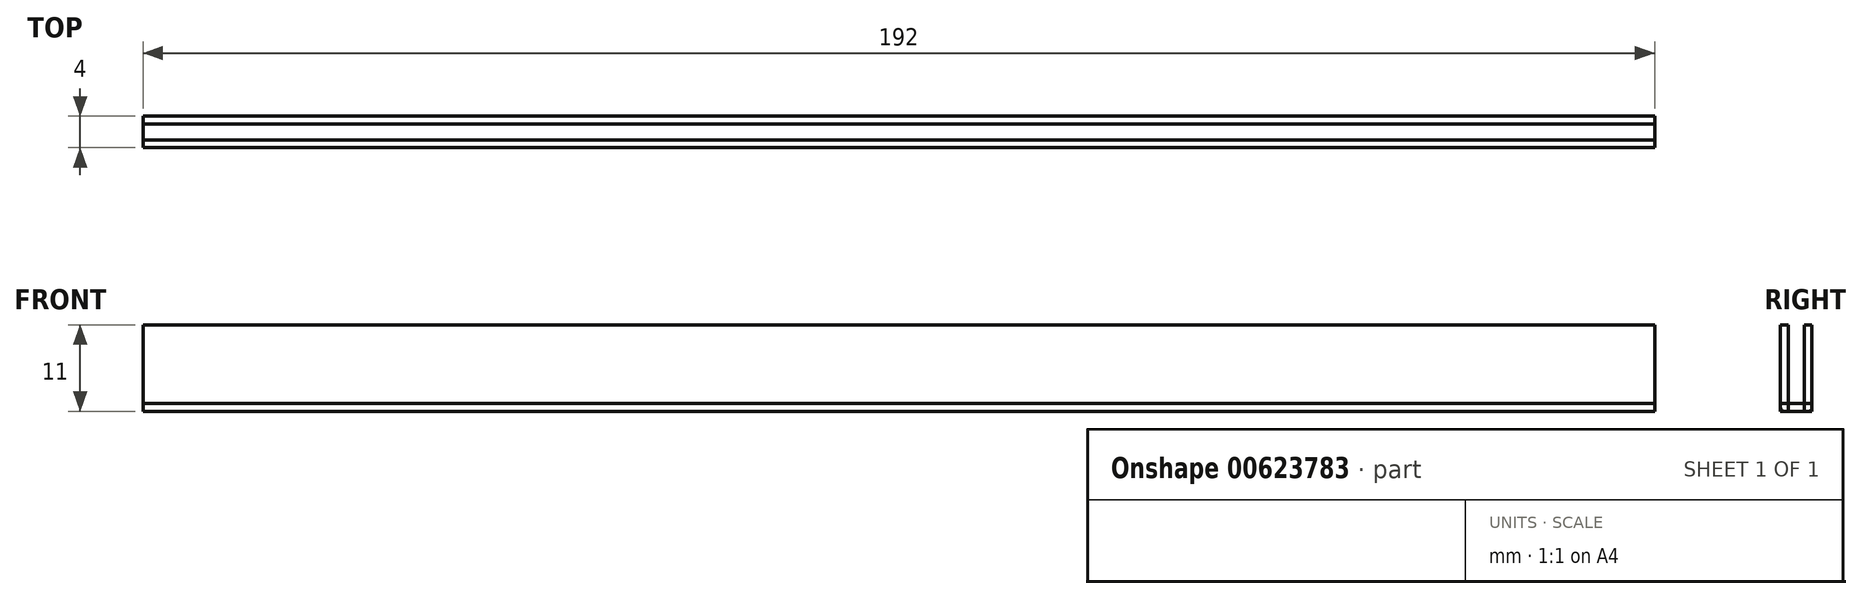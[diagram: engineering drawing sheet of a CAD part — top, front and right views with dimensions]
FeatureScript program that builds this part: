
annotation { "Feature Type Name" : "Feature", "Feature Type Description" : "" }
export const myFeature = defineFeature(function(context is Context, id is Id, definition is map)
    precondition{}
    {
        {
            var Q0;
            Q0=qCreatedBy(makeId("Top.planeOp"),FACE);
            var sketch = newSketch(context, id + "F0", { "sketchPlane" : qUnion([Q0])});
            skLineSegment(sketch, "E0.bottom", {"start": v(-97, -10) * mm, "end": v(95, -10) * mm});
            skLineSegment(sketch, "E0.top", {"start": v(-97, -14) * mm, "end": v(95, -14) * mm});
            skLineSegment(sketch, "E0.left", {"start": v(-97, -10) * mm, "end": v(-97, -14) * mm});
            skLineSegment(sketch, "E0.right", {"start": v(95, -10) * mm, "end": v(95, -14) * mm});
            skLineSegment(sketch, "E1", {"start": v(0, 0) * mm, "end": v(0, -10) * mm, "construction": true});
            skLineSegment(sketch, "E2", {"start": v(0, -10) * mm, "end": v(95, -10) * mm, "construction": true});
            skLineSegment(sketch, "E3.left", {"start": v(-97, -10) * mm, "end": v(-97, -10) * mm});
            skLineSegment(sketch, "E3.right", {"start": v(95, -10) * mm, "end": v(95, -10) * mm});
            skLineSegment(sketch, "E4.top", {"start": v(-97, -11) * mm, "end": v(95, -11) * mm});
            skLineSegment(sketch, "E4.left", {"start": v(-97, -10) * mm, "end": v(-97, -11) * mm});
            skLineSegment(sketch, "E4.right", {"start": v(95, -10) * mm, "end": v(95, -11) * mm});
            skLineSegment(sketch, "E5.top", {"start": v(-97, -13) * mm, "end": v(95, -13) * mm});
            skLineSegment(sketch, "E5.left", {"start": v(-97, -14) * mm, "end": v(-97, -13) * mm});
            skLineSegment(sketch, "E5.right", {"start": v(95, -14) * mm, "end": v(95, -13) * mm});
            skSolve(sketch);
        }
        {
            var Q0;
            Q0=makeQuery(id+"F0.imprint","IMPRINT",FACE,{"disambiguationData":[TD([[makeQuery(id+"F0.imprint","IMPRINT",EDGE,{"derivedFrom":sQuery(id+"F0.wireOp",EDGE,"E0.bottom")}),-1.0]])]});
            var Q1;
            Q1=makeQuery(id+"F0.imprint","IMPRINT",FACE,{"disambiguationData":[TD([[makeQuery(id+"F0.imprint","IMPRINT",EDGE,{"derivedFrom":sQuery(id+"F0.wireOp",EDGE,"E0.top")}),1.0]])]});
            extrude(context, id + "F1", {"entities" : qUnion([Q0, Q1]), "depth" : 11 * mm, "offsetDistance" : 25 * mm});
        }
        {
            var Q0;
            Q0=makeQuery(id+"F0.imprint","IMPRINT",FACE,{"disambiguationData":[TD([[makeQuery(id+"F0.imprint","IMPRINT",EDGE,{"derivedFrom":sQuery(id+"F0.wireOp",EDGE,"E0.left")}),1.0]])]});
            extrude(context, id + "F2", {"entities" : qUnion([Q0]), "depth" : 1 * mm, "offsetDistance" : 25 * mm});
        }
        {
            var Q0;
            Q0=makeQuery(id+"F1.opExtrude","CAP_EDGE",EDGE,{"disambiguationData":[OSD([sQuery(id+"F0.wireOp",EDGE,"E0.top")])],"isStart":true});
            var Q1;
            Q1=makeQuery(id+"F1.opExtrude","CAP_EDGE",EDGE,{"disambiguationData":[OSD([sQuery(id+"F0.wireOp",EDGE,"E0.bottom")])],"isStart":true});
            fillet(context, id + "F3", {"entities" : qUnion([Q0, Q1]), "radius" : .5 * mm, "tangentPropagation" : true, "allowEdgeOverflow" : false});
        }
    });
